# Revit family: QF_Vollrath_XLBC3-1826-13
name_source: partatom
category: Specialty Equipment
revit_build: Autodesk Revit 2016 (Build: 20151007_0715(x64)
units: mm (PartAtom-declared; Revit-internal decimal feet)

## family parameters
Always vertical = Yes
Cut with Voids When Loaded = No
OmniClass Number = 23.40.40.00
OmniClass Title = Food Service Equipment and Furnishings
Part Type = Normal
Room Calculation Point = No
Round Connector Dimension = Use Diameter
Shared = No
Work Plane-Based = No

## types (3) — shared parameters
Assembly Code = E1090300
CSI MasterFormat = 11 40 00
Description = Display Case
Foodservice Equipment Identifier = Yes
Manufacturer = Vollrath
URL = www.vollrath.com
zero-valued in all types: Weight in Pounds

## per-type parameters (varying)
| type | No Rear Doors | Rear Doors |
| XLBC3F-1826-13 | Yes | No |
| XLBC3FR-1826-13 | No | Yes |
| XLBC3P-1826-13 | No | Yes |

note: column(s) folded — value = type name in every type: Model

## geometry (parser evidence)
native form markers: Sweep x2
no freeform markers — native parametric forms only
